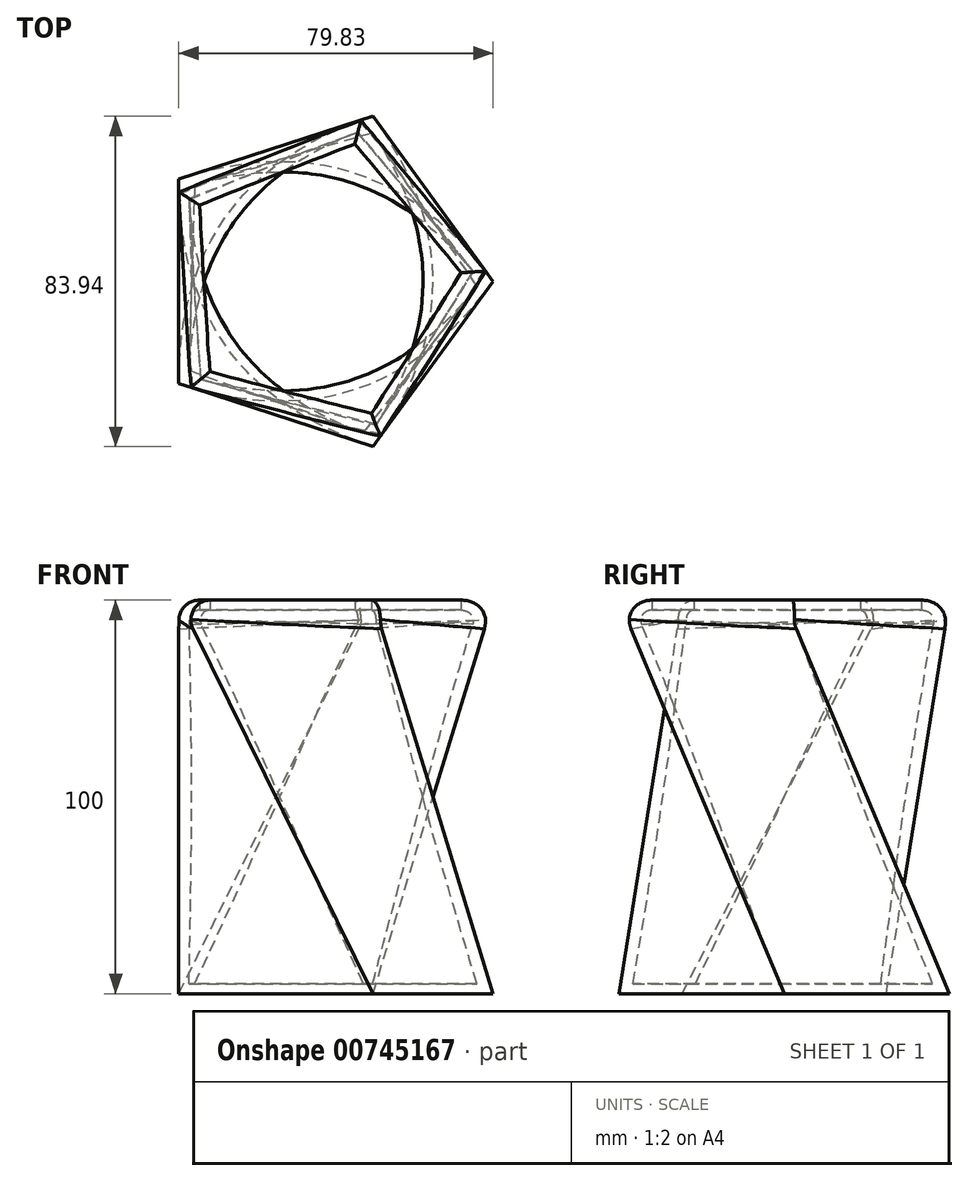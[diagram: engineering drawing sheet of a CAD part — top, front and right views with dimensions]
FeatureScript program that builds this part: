
annotation { "Feature Type Name" : "Feature", "Feature Type Description" : "" }
export const myFeature = defineFeature(function(context is Context, id is Id, definition is map)
    precondition{}
    {
        {
            var Q0;
            Q0=qCreatedBy(makeId("Top.planeOp"),FACE);
            cPlane(context, id + "F0", {"entities" : qUnion([Q0]), "cplaneType" : CPlaneType.OFFSET, "offset" : 100 * mm, "width" : 152.4 * mm, "height" : 152.4 * mm});
        }
        {
            var Q0;
            Q0=qCreatedBy(makeId("Top.planeOp"),FACE);
            var sketch = newSketch(context, id + "F1", { "sketchPlane" : qUnion([Q0])});
            skCircle(sketch, "E0.cCircle", {"center": v(0, 0) * mm, "radius": 35.7 * mm, "construction": true});
            skLineSegment(sketch, "E0.0", {"start": v(-35.7, -25.94) * mm, "end": v(-35.7, 25.94) * mm});
            skLineSegment(sketch, "E0.1", {"start": v(-35.7, 25.94) * mm, "end": v(13.64, 41.97) * mm});
            skLineSegment(sketch, "E0.2", {"start": v(13.64, 41.97) * mm, "end": v(44.13, 0) * mm});
            skLineSegment(sketch, "E0.3", {"start": v(44.13, 0) * mm, "end": v(13.64, -41.97) * mm});
            skLineSegment(sketch, "E0.4", {"start": v(13.64, -41.97) * mm, "end": v(-35.7, -25.94) * mm});
            skPoint(sketch, "E0.0.midPoint", {"position": v(-35.7, 0) * mm});
            skSolve(sketch);
        }
        {
            var Q0;
            Q0=qCreatedBy(id+"F0.planeOp",FACE);
            var sketch = newSketch(context, id + "F2", { "sketchPlane" : qUnion([Q0])});
            skLineSegment(sketch, "E1.0", {"start": v(13.64, 41.97) * mm, "end": v(44.13, 0) * mm});
            skLineSegment(sketch, "E2.0", {"start": v(44.13, 0) * mm, "end": v(13.64, -41.97) * mm});
            skLineSegment(sketch, "E3.0", {"start": v(13.64, -41.97) * mm, "end": v(-35.7, -25.94) * mm});
            skLineSegment(sketch, "E4.0", {"start": v(-35.7, -25.94) * mm, "end": v(-35.7, 25.94) * mm});
            skLineSegment(sketch, "E5.0", {"start": v(-35.7, 25.94) * mm, "end": v(13.64, 41.97) * mm});
            skSolve(sketch);
        }
        {
            var Q0;
            Q0=makeQuery(id+"F1.imprint","IMPRINT",FACE,{"disambiguationData":[TD([[makeQuery(id+"F1.imprint","IMPRINT",EDGE,{"derivedFrom":sQuery(id+"F1.wireOp",EDGE,"E0.0")}),-1.0]])]});
            var Q1;
            Q1=makeQuery(id+"F2.imprint","IMPRINT",FACE,{"disambiguationData":[TD([[makeQuery(id+"F2.imprint","IMPRINT",EDGE,{"derivedFrom":sQuery(id+"F2.wireOp",EDGE,"E1.0")}),-1.0]])]});
            var Q2;
            Q2=sQuery(id+"F2.wireOp",VERTEX,"E5.0.start");
            var Q3;
            Q3=sQuery(id+"F1.wireOp",VERTEX,"E0.0.start");
            loft(context, id + "F3", {"sheetProfilesArray" : [{ "sheetProfileEntities" : qUnion([Q0]) }, { "sheetProfileEntities" : qUnion([Q1]) }], "matchConnections" : true, "connections" : [{ "connectionEntities" : qUnion([Q2, Q3]), "connectionEdgeQueries" : qUnion([]), "connectionEdgeParameters" : [] }]});
        }
        {
            var Q0;
            Q0=makeQuery(id+"F3.opLoft","CAP_FACE",FACE,{"disambiguationData":[OSD([makeQuery(id+"F2.imprint","IMPRINT",FACE,{"disambiguationData":[TD([[makeQuery(id+"F2.imprint","IMPRINT",EDGE,{"derivedFrom":sQuery(id+"F2.wireOp",EDGE,"E1.0")}),-1.0]])]})])],"isStart":true});
            fillet(context, id + "F4", {"entities" : qUnion([Q0]), "radius" : 5.08 * mm, "tangentPropagation" : true, "allowEdgeOverflow" : false});
        }
        {
            var Q0;
            Q0=makeQuery(id+"F3.opLoft","CAP_FACE",FACE,{"disambiguationData":[OSD([makeQuery(id+"F2.imprint","IMPRINT",FACE,{"disambiguationData":[TD([[makeQuery(id+"F2.imprint","IMPRINT",EDGE,{"derivedFrom":sQuery(id+"F2.wireOp",EDGE,"E1.0")}),-1.0]])]})])],"isStart":true});
            shell(context, id + "F5", {"entities" : qUnion([Q0]), "thickness" : 2.54 * mm});
        }
    });
